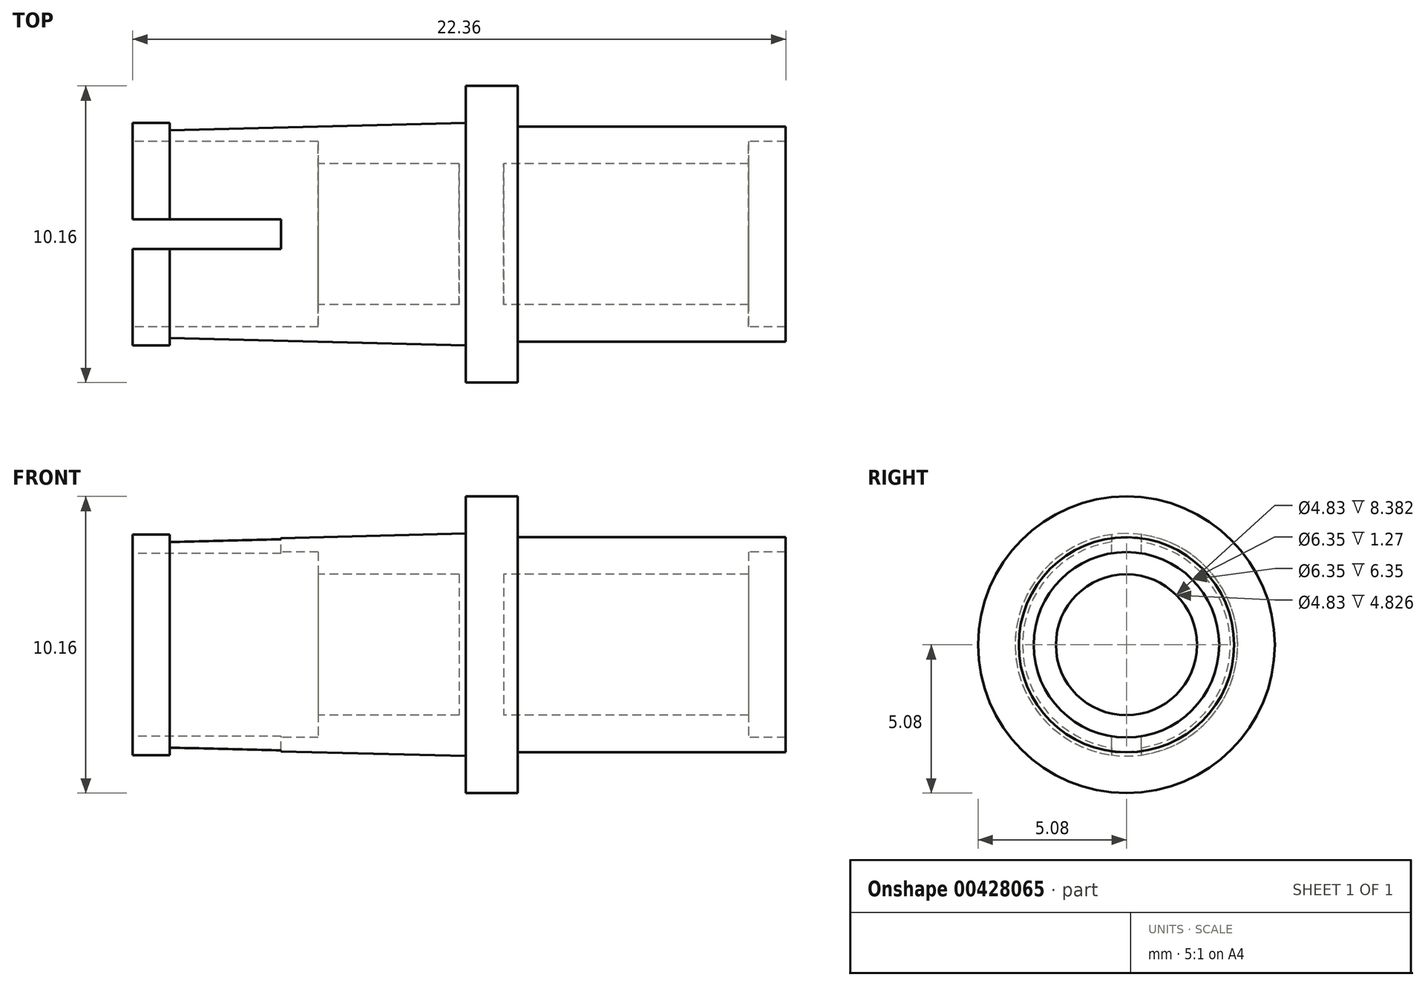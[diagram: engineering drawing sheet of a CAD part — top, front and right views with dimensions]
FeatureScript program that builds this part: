
annotation { "Feature Type Name" : "Feature", "Feature Type Description" : "" }
export const myFeature = defineFeature(function(context is Context, id is Id, definition is map)
    precondition{}
    {
        {
            var Q0;
            Q0=qCreatedBy(makeId("Front.planeOp"),FACE);
            var sketch = newSketch(context, id + "F0", { "sketchPlane" : qUnion([Q0])});
            skLineSegment(sketch, "E0", {"start": v(0, 0) * mm, "end": v(0, 2.41) * mm});
            skLineSegment(sketch, "E1", {"start": v(0, 2.41) * mm, "end": v(-4.83, 2.41) * mm});
            skLineSegment(sketch, "E2", {"start": v(-4.83, 2.41) * mm, "end": v(-4.83, 3.18) * mm});
            skLineSegment(sketch, "E3", {"start": v(-4.83, 3.18) * mm, "end": v(-11.18, 3.17) * mm});
            skLineSegment(sketch, "E4", {"start": v(-11.18, 3.17) * mm, "end": v(-11.18, 3.81) * mm});
            skLineSegment(sketch, "E5", {"start": v(-11.18, 3.81) * mm, "end": v(-9.9, 3.81) * mm});
            skLineSegment(sketch, "E6", {"start": v(-9.9, 3.81) * mm, "end": v(-9.9, 3.56) * mm});
            skLineSegment(sketch, "E7", {"start": v(-9.9, 3.56) * mm, "end": v(0.23, 3.81) * mm});
            skLineSegment(sketch, "E8", {"start": v(0.23, 3.81) * mm, "end": v(0.23, 5.08) * mm});
            skLineSegment(sketch, "E9", {"start": v(0.23, 5.08) * mm, "end": v(2, 5.08) * mm});
            skLineSegment(sketch, "E10", {"start": v(2, 5.08) * mm, "end": v(2, 3.68) * mm});
            skLineSegment(sketch, "E11", {"start": v(2, 3.68) * mm, "end": v(11.18, 3.68) * mm});
            skLineSegment(sketch, "E12", {"start": v(11.18, 3.68) * mm, "end": v(11.18, 3.18) * mm});
            skLineSegment(sketch, "E13", {"start": v(11.18, 3.18) * mm, "end": v(9.9, 3.18) * mm});
            skLineSegment(sketch, "E14", {"start": v(9.9, 3.18) * mm, "end": v(9.9, 2.41) * mm});
            skLineSegment(sketch, "E15", {"start": v(9.9, 2.41) * mm, "end": v(1.52, 2.41) * mm});
            skLineSegment(sketch, "E16", {"start": v(1.52, 2.41) * mm, "end": v(1.52, 0) * mm});
            skLineSegment(sketch, "E17", {"start": v(1.52, 0) * mm, "end": v(0, 0) * mm});
            skLineSegment(sketch, "E18", {"start": v(-20.77, 0) * mm, "end": v(10.16, 0) * mm, "construction": true});
            skSolve(sketch);
        }
        {
            var Q0;
            Q0=makeQuery(id+"F0.imprint","IMPRINT",FACE,{"disambiguationData":[TD([[makeQuery(id+"F0.imprint","IMPRINT",EDGE,{"derivedFrom":sQuery(id+"F0.wireOp",EDGE,"E0")}),-1.0]])]});
            var Q1;
            Q1=sQuery(id+"F0.wireOp",EDGE,"E18");
            revolve(context, id + "F1", {"entities" : qUnion([Q0]), "axis" : qUnion([Q1]), "revolveType" : RevolveType.FULL});
        }
        {
            var Q0;
            Q0=qCreatedBy(makeId("Top.planeOp"),FACE);
            var sketch = newSketch(context, id + "F2", { "sketchPlane" : qUnion([Q0])});
            skLineSegment(sketch, "E19.bottom", {"start": v(-11.18, -0.5) * mm, "end": v(-6.1, -0.5) * mm});
            skLineSegment(sketch, "E19.top", {"start": v(-11.18, 0.5) * mm, "end": v(-6.1, 0.5) * mm});
            skLineSegment(sketch, "E19.left", {"start": v(-11.18, -0.5) * mm, "end": v(-11.18, 0.5) * mm});
            skLineSegment(sketch, "E19.right", {"start": v(-6.1, -0.5) * mm, "end": v(-6.1, 0.5) * mm});
            skSolve(sketch);
        }
        {
            var Q0;
            Q0=makeQuery(id+"F2.imprint","IMPRINT",FACE,{"disambiguationData":[TD([[makeQuery(id+"F2.imprint","IMPRINT",EDGE,{"derivedFrom":sQuery(id+"F2.wireOp",EDGE,"E19.bottom")}),1.0]])]});
            extrude(context, id + "F3", {"entities" : qUnion([Q0]), "operationType" : NewBodyOperationType.REMOVE, "oppositeDirection" : true, "depth" : 25.4 * mm, "hasSecondDirection" : true, "secondDirectionOppositeDirection" : false, "secondDirectionDepth" : 25.4 * mm});
        }
    });
